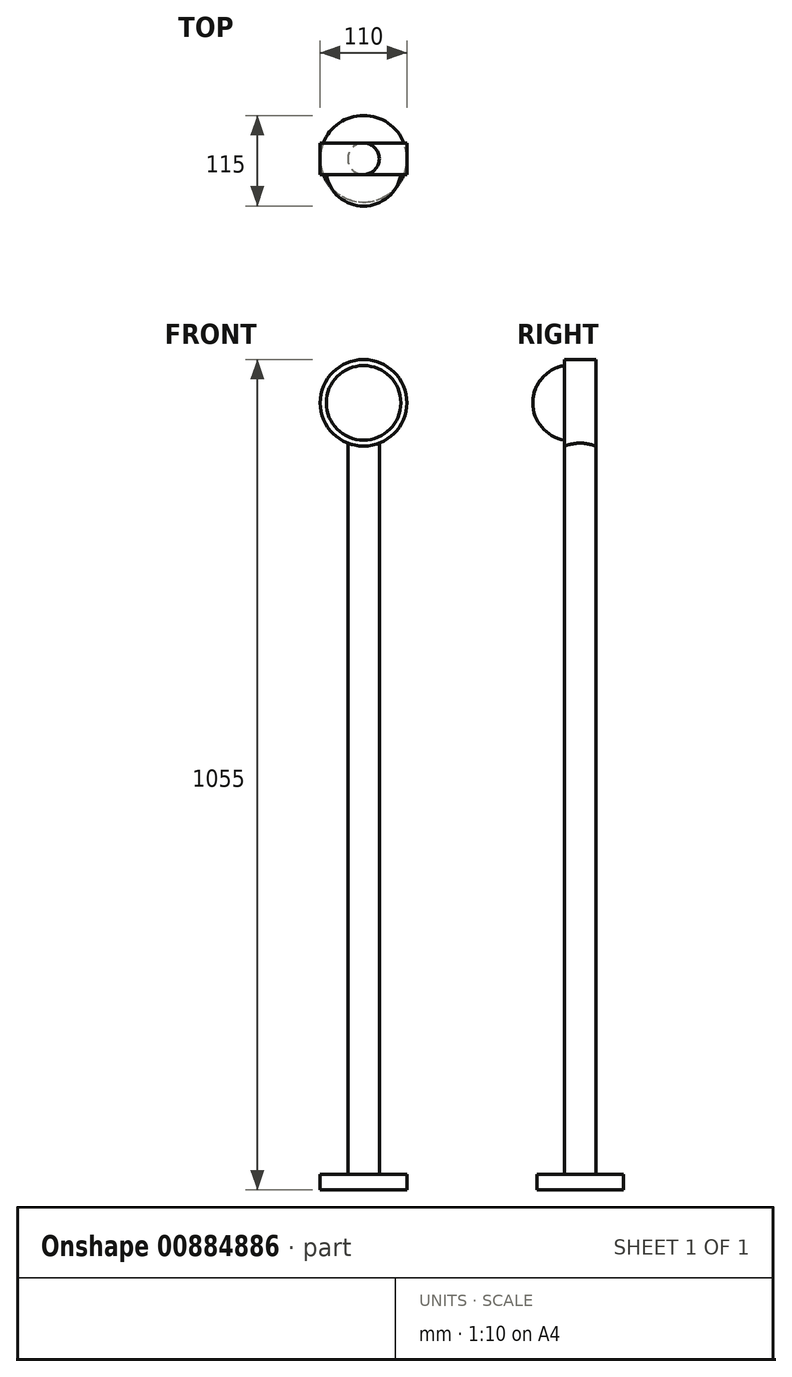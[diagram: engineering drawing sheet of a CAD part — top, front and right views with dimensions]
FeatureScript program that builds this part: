
annotation { "Feature Type Name" : "Feature", "Feature Type Description" : "" }
export const myFeature = defineFeature(function(context is Context, id is Id, definition is map)
    precondition{}
    {
        {
            var Q0;
            Q0=qCreatedBy(makeId("Right.planeOp"),FACE);
            var sketch = newSketch(context, id + "F0", { "sketchPlane" : qUnion([Q0])});
            skLineSegment(sketch, "E0", {"start": v(0, 0) * mm, "end": v(-55, 0) * mm});
            skLineSegment(sketch, "E1", {"start": v(-55, 0) * mm, "end": v(-55, 20) * mm});
            skLineSegment(sketch, "E2", {"start": v(-55, 20) * mm, "end": v(-20, 20) * mm});
            skLineSegment(sketch, "E3", {"start": v(-20, 20) * mm, "end": v(-20, 1000) * mm});
            skLineSegment(sketch, "E4", {"start": v(-20, 1000) * mm, "end": v(0, 1000) * mm});
            skLineSegment(sketch, "E5", {"start": v(0, 1000) * mm, "end": v(0, 0) * mm});
            skSolve(sketch);
        }
        {
            var Q0;
            Q0=makeQuery(id+"F0.imprint","IMPRINT",FACE,{"disambiguationData":[TD([[makeQuery(id+"F0.imprint","IMPRINT",EDGE,{"derivedFrom":sQuery(id+"F0.wireOp",EDGE,"E0")}),-1.0]])]});
            var Q1;
            Q1=sQuery(id+"F0.wireOp",EDGE,"E5");
            revolve(context, id + "F1", {"surfaceOperationType" : NewSurfaceOperationType.NEW, "entities" : qUnion([Q0]), "axis" : qUnion([Q1]), "revolveType" : RevolveType.FULL});
        }
        {
            var Q0;
            Q0=qCreatedBy(makeId("Front.planeOp"),FACE);
            var sketch = newSketch(context, id + "F2", { "sketchPlane" : qUnion([Q0])});
            skCircle(sketch, "E6", {"center": v(0, 1000) * mm, "radius": 55 * mm});
            skSolve(sketch);
        }
        {
            var Q0;
            Q0=makeQuery(id+"F2.imprint","IMPRINT",FACE,{"disambiguationData":[TD([[makeQuery(id+"F2.imprint","IMPRINT",EDGE,{"derivedFrom":sQuery(id+"F2.wireOp",EDGE,"E6")}),1.0]])]});
            extrude(context, id + "F3", {"entities" : qUnion([Q0]), "operationType" : NewBodyOperationType.ADD, "endBound" : BoundingType.SYMMETRIC, "depth" : 40 * mm, "offsetDistance" : 25 * mm});
        }
        {
            var Q0;
            Q0=qCreatedBy(makeId("Right.planeOp"),FACE);
            var sketch = newSketch(context, id + "F4", { "sketchPlane" : qUnion([Q0])});
            skArc(sketch, "E7", {"start": v(-12, 1048) * mm, "mid": v(-45.94, 1033.94) * mm, "end": v(-60, 1000) * mm});
            skLineSegment(sketch, "E8", {"start": v(-12, 1048) * mm, "end": v(-12, 1000) * mm});
            skLineSegment(sketch, "E9", {"start": v(-60, 1000) * mm, "end": v(-12, 1000) * mm});
            skSolve(sketch);
        }
        {
            var Q0;
            Q0=makeQuery(id+"F4.imprint","IMPRINT",FACE,{"disambiguationData":[TD([[makeQuery(id+"F4.imprint","IMPRINT",EDGE,{"derivedFrom":sQuery(id+"F4.wireOp",EDGE,"E7")}),1.0]])]});
            var Q1;
            Q1=sQuery(id+"F4.wireOp",EDGE,"E9");
            revolve(context, id + "F5", {"operationType" : NewBodyOperationType.ADD, "surfaceOperationType" : NewSurfaceOperationType.NEW, "entities" : qUnion([Q0]), "axis" : qUnion([Q1]), "revolveType" : RevolveType.FULL});
        }
    });
